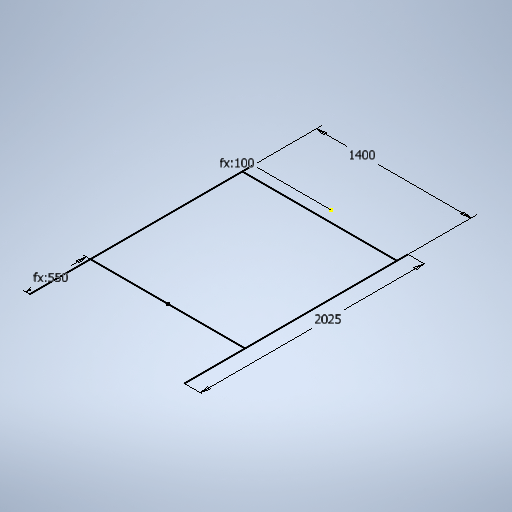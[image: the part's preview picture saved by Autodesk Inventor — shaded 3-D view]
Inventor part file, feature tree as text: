
AUTODESK INVENTOR PART (.ipt)
format: ipt  version: 2025 (Build 290162010, 162A)  size: 259,072 bytes
history: native  units: in
note: dims shown in document units (in); Inventor stores cm internally (conversion verified against a paired STEP export)
features: sketch x1
ambient origin geometry x8: Origin, YZ Plane, XZ Plane, XY Plane, X Axis, Y Axis, Z Axis, Center Point
feature tree (1):
  sketch  "Sketch3"  dims[d7=55.1181in d9=79.7244in d11=21.6535in d12=3.937in]
